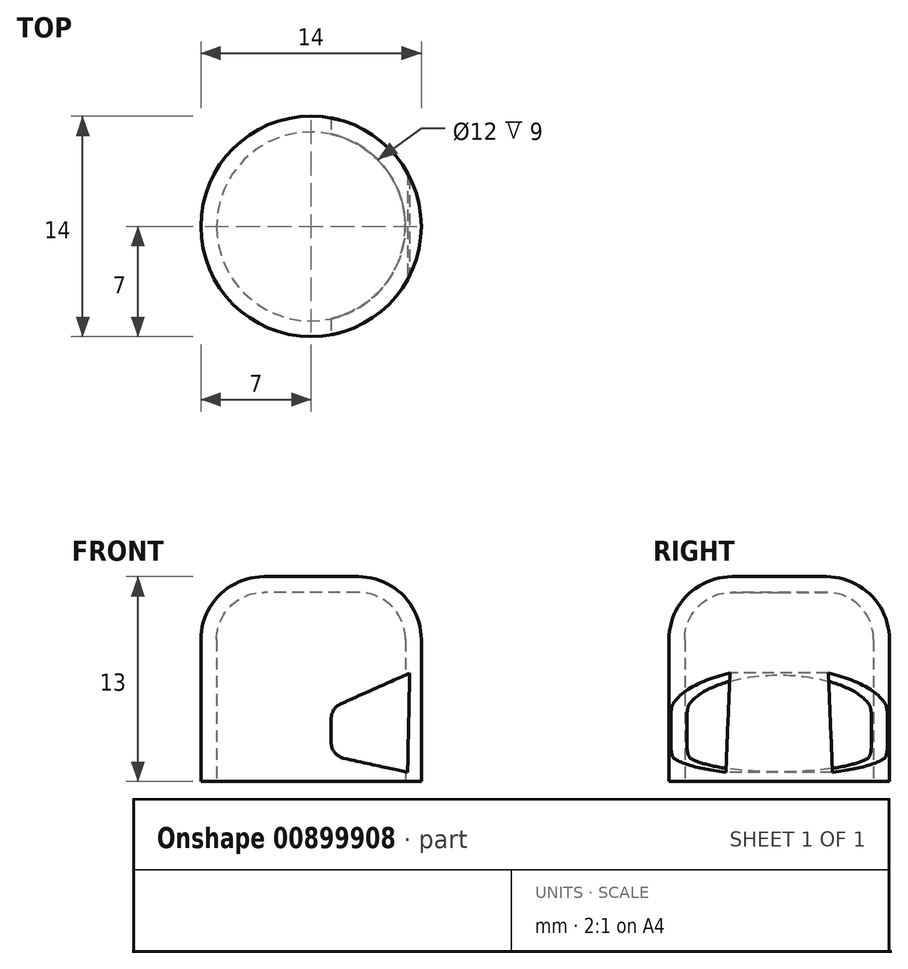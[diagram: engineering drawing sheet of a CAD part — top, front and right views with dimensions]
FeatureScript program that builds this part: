
annotation { "Feature Type Name" : "Feature", "Feature Type Description" : "" }
export const myFeature = defineFeature(function(context is Context, id is Id, definition is map)
    precondition{}
    {
        {
            var Q0;
            Q0=qCreatedBy(makeId("Top.planeOp"),FACE);
            var sketch = newSketch(context, id + "F0", { "sketchPlane" : qUnion([Q0])});
            skCircle(sketch, "E0", {"center": v(0, 0) * mm, "radius": 7 * mm});
            skSolve(sketch);
        }
        {
            var Q0;
            Q0 = qSketchRegion(id + "F0", true);
            extrude(context, id + "F1", {"entities" : qUnion([Q0]), "depth" : 13 * mm, "offsetDistance" : 25.4 * mm});
        }
        {
            var Q0;
            Q0=makeQuery(id+"F1.opExtrude","CAP_EDGE",EDGE,{"disambiguationData":[OSD([sQuery(id+"F0.wireOp",EDGE,"E0")])],"isStart":false});
            fillet(context, id + "F2", {"entities" : qUnion([Q0]), "radius" : 4 * mm, "tangentPropagation" : true, "allowEdgeOverflow" : false});
        }
        {
            var Q0;
            Q0=makeQuery(id+"F1.opExtrude","CAP_FACE",FACE,{"disambiguationData":[OSD([sQuery(id+"F0.wireOp",EDGE,"E0")])],"isStart":true});
            shell(context, id + "F3", {"entities" : qUnion([Q0]), "thickness" : 1 * mm});
        }
        {
            var Q0;
            Q0=qCreatedBy(makeId("Front.planeOp"),FACE);
            var sketch = newSketch(context, id + "F4", { "sketchPlane" : qUnion([Q0])});
            skLineSegment(sketch, "E1", {"start": v(6.26, 6.87) * mm, "end": v(1.87, 4.91) * mm});
            skLineSegment(sketch, "E2", {"start": v(2.06, 1.47) * mm, "end": v(6.13, 0.57) * mm});
            skLineSegment(sketch, "E3", {"start": v(6.13, 0.57) * mm, "end": v(6.26, 6.87) * mm});
            skLineSegment(sketch, "E4", {"start": v(1.28, 4) * mm, "end": v(1.28, 2.44) * mm});
            skPoint(sketch, "E5.visualSharp", {"position": v(1.28, 4.65) * mm});
            skArc(sketch, "E5.filletArc", {"start": v(1.87, 4.91) * mm, "mid": v(1.44, 4.54) * mm, "end": v(1.28, 4) * mm});
            skPoint(sketch, "E6.visualSharp", {"position": v(1.28, 1.64) * mm});
            skArc(sketch, "E6.filletArc", {"start": v(1.28, 2.44) * mm, "mid": v(1.5, 1.82) * mm, "end": v(2.06, 1.47) * mm});
            skSolve(sketch);
        }
        {
            var Q0;
            Q0=makeQuery(id+"F4.imprint","IMPRINT",FACE,{"disambiguationData":[TD([[makeQuery(id+"F4.imprint","IMPRINT",EDGE,{"derivedFrom":sQuery(id+"F4.wireOp",EDGE,"E1")}),1.0]])]});
            extrude(context, id + "F5", {"entities" : qUnion([Q0]), "operationType" : NewBodyOperationType.REMOVE, "endBound" : BoundingType.SYMMETRIC, "oppositeDirection" : true, "depth" : 25 * mm, "offsetDistance" : 25.4 * mm});
        }
    });
